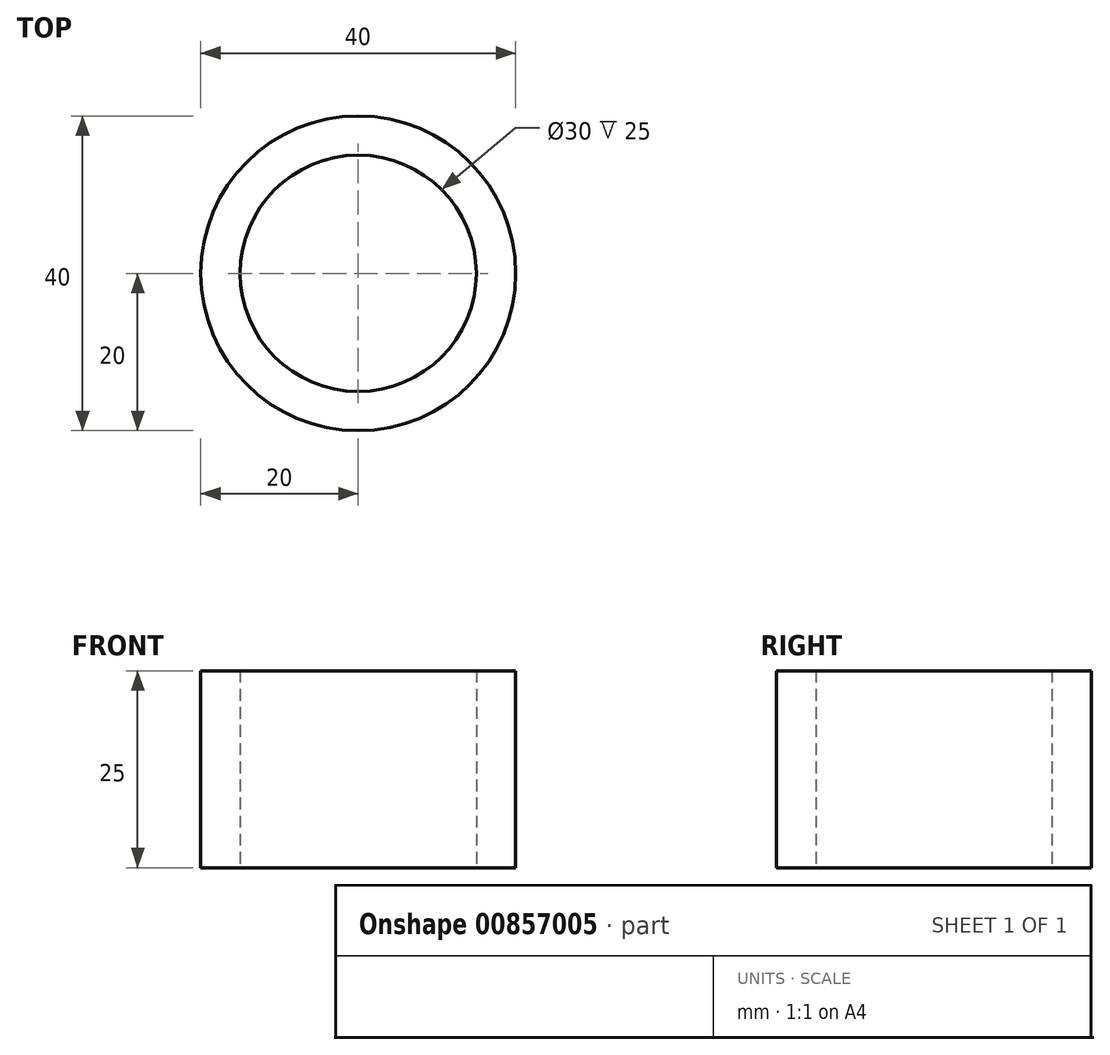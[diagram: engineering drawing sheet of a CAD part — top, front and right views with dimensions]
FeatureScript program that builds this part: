
annotation { "Feature Type Name" : "Feature", "Feature Type Description" : "" }
export const myFeature = defineFeature(function(context is Context, id is Id, definition is map)
    precondition{}
    {
        {
            var Q0;
            Q0=qCreatedBy(makeId("Top.planeOp"),FACE);
            var sketch = newSketch(context, id + "F0", { "sketchPlane" : qUnion([Q0])});
            skCircle(sketch, "E0", {"center": v(0, 0) * mm, "radius": 20 * mm});
            skCircle(sketch, "E1", {"center": v(0, 0) * mm, "radius": 15 * mm});
            skSolve(sketch);
        }
        {
            var Q0;
            Q0 = qSketchRegion(id + "F0", true);
            extrude(context, id + "F1", {"entities" : qUnion([Q0]), "depth" : 25 * mm, "offsetDistance" : 25 * mm});
        }
    });
